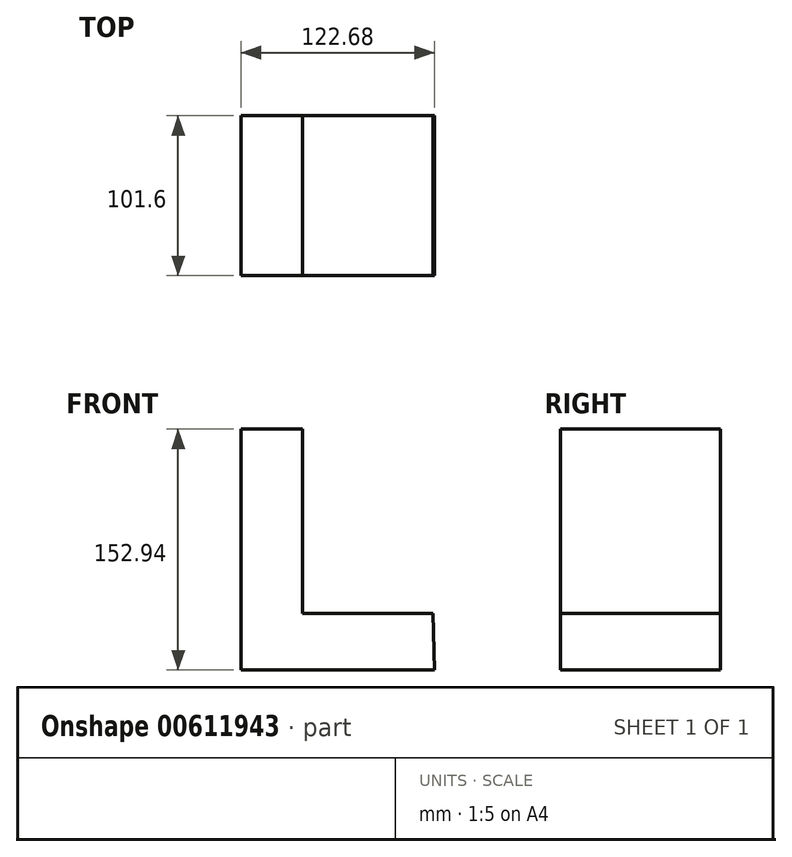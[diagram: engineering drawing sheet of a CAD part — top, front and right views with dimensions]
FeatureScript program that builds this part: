
annotation { "Feature Type Name" : "Feature", "Feature Type Description" : "" }
export const myFeature = defineFeature(function(context is Context, id is Id, definition is map)
    precondition{}
    {
        {
            var Q0;
            Q0=qCreatedBy(makeId("Front.planeOp"),FACE);
            var sketch = newSketch(context, id + "F0", { "sketchPlane" : qUnion([Q0])});
            skLineSegment(sketch, "E0", {"start": v(0, 76.32) * mm, "end": v(0, -76.62) * mm});
            skLineSegment(sketch, "E1", {"start": v(0, -76.62) * mm, "end": v(122.68, -76.62) * mm});
            skLineSegment(sketch, "E2", {"start": v(122.68, -76.62) * mm, "end": v(121.9, -40.9) * mm});
            skLineSegment(sketch, "E3", {"start": v(121.9, -40.9) * mm, "end": v(39, -40.9) * mm});
            skLineSegment(sketch, "E4", {"start": v(39, -40.9) * mm, "end": v(39, 76.26) * mm});
            skLineSegment(sketch, "E5", {"start": v(39, 76.26) * mm, "end": v(0, 76.32) * mm});
            skSolve(sketch);
        }
        {
            var Q0;
            Q0=makeQuery(id+"F0.imprint","IMPRINT",FACE,{"disambiguationData":[TD([[makeQuery(id+"F0.imprint","IMPRINT",EDGE,{"derivedFrom":sQuery(id+"F0.wireOp",EDGE,"E0")}),1.0]])]});
            extrude(context, id + "F1", {"entities" : qUnion([Q0]), "endBound" : BoundingType.SYMMETRIC, "oppositeDirection" : true, "depth" : 101.6 * mm, "offsetDistance" : 25.4 * mm});
        }
    });
